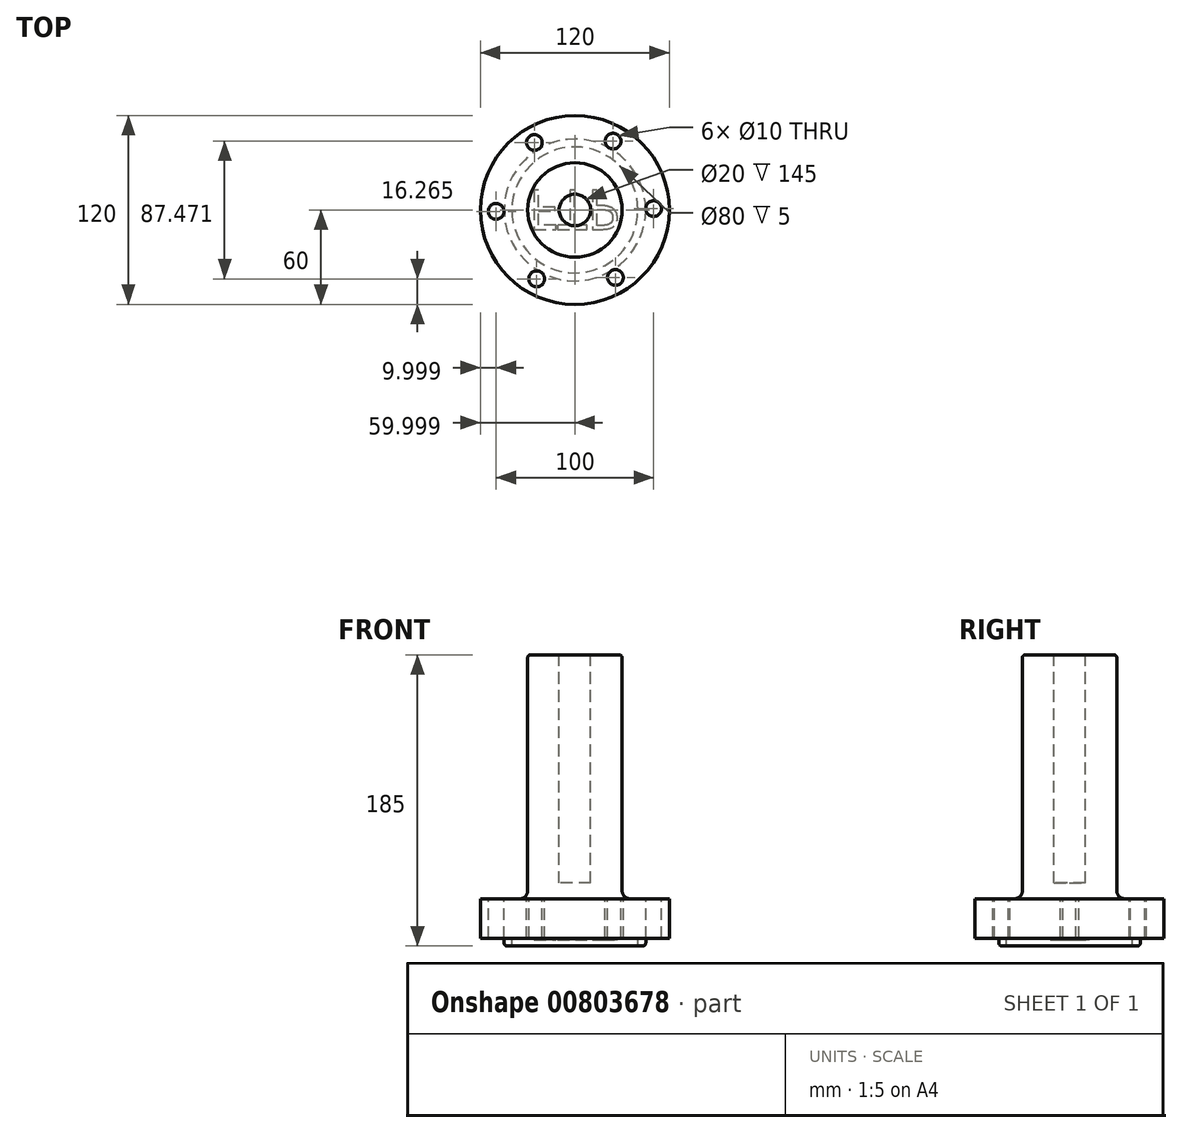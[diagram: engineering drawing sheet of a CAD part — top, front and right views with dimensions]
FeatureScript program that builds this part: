
annotation { "Feature Type Name" : "Feature", "Feature Type Description" : "" }
export const myFeature = defineFeature(function(context is Context, id is Id, definition is map)
    precondition{}
    {
        {
            var Q0;
            Q0=qCreatedBy(makeId("Front.planeOp"),FACE);
            var sketch = newSketch(context, id + "F0", { "sketchPlane" : qUnion([Q0])});
            skLineSegment(sketch, "E0", {"start": v(158.82, 97.64) * mm, "end": v(158.82, -82.36) * mm});
            skLineSegment(sketch, "E1", {"start": v(158.82, -82.36) * mm, "end": v(218.82, -82.36) * mm});
            skLineSegment(sketch, "E2", {"start": v(218.82, -82.36) * mm, "end": v(218.82, -57.36) * mm});
            skLineSegment(sketch, "E3", {"start": v(218.82, -57.36) * mm, "end": v(188.82, -57.36) * mm});
            skLineSegment(sketch, "E4", {"start": v(188.82, -57.36) * mm, "end": v(188.82, 97.64) * mm});
            skLineSegment(sketch, "E5", {"start": v(188.82, 97.64) * mm, "end": v(158.82, 97.64) * mm});
            skSolve(sketch);
        }
        {
            var Q0;
            Q0 = qSketchRegion(id + "F0", true);
            var Q1;
            Q1=sQuery(id+"F0.wireOp",EDGE,"E0");
            revolve(context, id + "F1", {"surfaceOperationType" : NewSurfaceOperationType.NEW, "entities" : qUnion([Q0]), "axis" : qUnion([Q1]), "revolveType" : RevolveType.FULL});
        }
        {
            var Q0;
            Q0=makeQuery(id+"F1.opRevolve","SWEPT_FACE",FACE,{"disambiguationData":[OSD([sQuery(id+"F0.wireOp",EDGE,"E5")])]});
            var sketch = newSketch(context, id + "F2", { "sketchPlane" : qUnion([Q0])});
            skCircle(sketch, "E6", {"center": v(158.82, 0) * mm, "radius": 10 * mm});
            skSolve(sketch);
        }
        {
            var Q0;
            Q0 = qSketchRegion(id + "F2", true);
            extrude(context, id + "F3", {"entities" : qUnion([Q0]), "operationType" : NewBodyOperationType.REMOVE, "oppositeDirection" : true, "depth" : 145 * mm, "offsetDistance" : 25 * mm});
        }
        {
            var Q0;
            Q0=makeQuery(id+"F1.opRevolve","SWEPT_FACE",FACE,{"disambiguationData":[OSD([sQuery(id+"F0.wireOp",EDGE,"E3")])]});
            var sketch = newSketch(context, id + "F4", { "sketchPlane" : qUnion([Q0])});
            skCircle(sketch, "E7", {"center": v(133.07, 42.87) * mm, "radius": 5 * mm});
            skCircle(sketch, "E8.1.0", {"center": v(108.82, -0.87) * mm, "radius": 5 * mm});
            skCircle(sketch, "E8.2.0", {"center": v(134.57, -43.74) * mm, "radius": 5 * mm});
            skCircle(sketch, "E8.3.0", {"center": v(184.57, -42.87) * mm, "radius": 5 * mm});
            skCircle(sketch, "E8.4.0", {"center": v(208.82, 0.87) * mm, "radius": 5 * mm});
            skCircle(sketch, "E8.5.0", {"center": v(183.07, 43.74) * mm, "radius": 5 * mm});
            skPoint(sketch, "E8.center", {"position": v(158.82, 0) * mm});
            skCircle(sketch, "E9", {"center": v(158.82, 0) * mm, "radius": 35 * mm});
            skSolve(sketch);
        }
        {
            var Q0;
            Q0=makeQuery(id+"F4.imprint","IMPRINT",FACE,{"disambiguationData":[TD([[makeQuery(id+"F4.imprint","IMPRINT",EDGE,{"derivedFrom":sQuery(id+"F4.wireOp",EDGE,"E7")}),1.0]])]});
            var Q1;
            Q1=makeQuery(id+"F4.imprint","IMPRINT",FACE,{"disambiguationData":[TD([[makeQuery(id+"F4.imprint","IMPRINT",EDGE,{"derivedFrom":sQuery(id+"F4.wireOp",EDGE,"E8.5.0")}),1.0]])]});
            var Q2;
            Q2=makeQuery(id+"F4.imprint","IMPRINT",FACE,{"disambiguationData":[TD([[makeQuery(id+"F4.imprint","IMPRINT",EDGE,{"derivedFrom":sQuery(id+"F4.wireOp",EDGE,"E8.4.0")}),1.0]])]});
            var Q3;
            Q3=makeQuery(id+"F4.imprint","IMPRINT",FACE,{"disambiguationData":[TD([[makeQuery(id+"F4.imprint","IMPRINT",EDGE,{"derivedFrom":sQuery(id+"F4.wireOp",EDGE,"E8.3.0")}),1.0]])]});
            var Q4;
            Q4=makeQuery(id+"F4.imprint","IMPRINT",FACE,{"disambiguationData":[TD([[makeQuery(id+"F4.imprint","IMPRINT",EDGE,{"derivedFrom":sQuery(id+"F4.wireOp",EDGE,"E8.1.0")}),1.0]])]});
            var Q5;
            Q5=makeQuery(id+"F4.imprint","IMPRINT",FACE,{"disambiguationData":[TD([[makeQuery(id+"F4.imprint","IMPRINT",EDGE,{"derivedFrom":sQuery(id+"F4.wireOp",EDGE,"E8.2.0")}),1.0]])]});
            var Q6;
            Q6=sQuery(id+"F4.wireOp",EDGE,"E7");
            var Q7;
            Q7=sQuery(id+"F4.wireOp",EDGE,"E8.5.0");
            var Q8;
            Q8=sQuery(id+"F4.wireOp",EDGE,"E8.4.0");
            var Q9;
            Q9=sQuery(id+"F4.wireOp",EDGE,"E8.3.0");
            var Q10;
            Q10=sQuery(id+"F4.wireOp",EDGE,"E8.2.0");
            var Q11;
            Q11=sQuery(id+"F4.wireOp",EDGE,"E8.1.0");
            extrude(context, id + "F5", {"entities" : qUnion([Q0, Q1, Q2, Q3, Q4, Q5]), "operationType" : NewBodyOperationType.REMOVE, "surfaceEntities" : qUnion([Q6, Q7, Q8, Q9, Q10, Q11]), "oppositeDirection" : true, "depth" : 25 * mm, "offsetDistance" : 25 * mm});
        }
        {
            var Q0;
            Q0=makeQuery(id+"F1.opRevolve","SWEPT_FACE",FACE,{"disambiguationData":[OSD([sQuery(id+"F0.wireOp",EDGE,"E1")])]});
            var sketch = newSketch(context, id + "F6", { "sketchPlane" : qUnion([Q0])});
            skCircle(sketch, "E10", {"center": v(158.82, 0) * mm, "radius": 45 * mm});
            skCircle(sketch, "E11", {"center": v(158.82, 0) * mm, "radius": 40 * mm});
            skSolve(sketch);
        }
        {
            var Q0;
            Q0=makeQuery(id+"F6.imprint","IMPRINT",FACE,{"disambiguationData":[TD([[makeQuery(id+"F6.imprint","IMPRINT",EDGE,{"derivedFrom":sQuery(id+"F6.wireOp",EDGE,"E10")}),1.0]])]});
            extrude(context, id + "F7", {"entities" : qUnion([Q0]), "operationType" : NewBodyOperationType.ADD, "depth" : 5 * mm, "offsetDistance" : 25 * mm});
        }
        {
            var Q0;
            Q0=makeQuery(id+"F1.opRevolve","SWEPT_EDGE",EDGE,{"disambiguationData":[OSD([sQuery(id+"F0.wireOp",EDGE,"E3"),sQuery(id+"F0.wireOp",EDGE,"E4")])]});
            fillet(context, id + "F8", {"entities" : qUnion([Q0]), "radius" : 5 * mm, "tangentPropagation" : true, "allowEdgeOverflow" : false});
        }
        {
            var Q0;
            Q0=makeQuery(id+"F1.opRevolve","SWEPT_EDGE",EDGE,{"disambiguationData":[OSD([sQuery(id+"F0.wireOp",EDGE,"E4"),sQuery(id+"F0.wireOp",EDGE,"E5")])]});
            fillet(context, id + "F9", {"entities" : qUnion([Q0]), "radius" : 2 * mm, "tangentPropagation" : true, "allowEdgeOverflow" : false});
        }
        {
            var Q0;
            Q0=makeQuery(id+"F7.opExtrude","CAP_EDGE",EDGE,{"disambiguationData":[OSD([sQuery(id+"F6.wireOp",EDGE,"E10")])],"isStart":false});
            fillet(context, id + "F10", {"entities" : qUnion([Q0]), "radius" : 2 * mm, "tangentPropagation" : true, "allowEdgeOverflow" : false});
        }
        {
            var Q0;
            Q0=makeQuery(id+"F7.boolean.opBoolean","SPLIT",FACE,{"disambiguationData":[TD([makeQuery(id+"F7.opExtrude","SWEPT_FACE",FACE,{"disambiguationData":[OSD([sQuery(id+"F6.wireOp",EDGE,"E11")])]})])],"derivedFrom":makeQuery(id+"F1.opRevolve","SWEPT_FACE",FACE,{"disambiguationData":[OSD([sQuery(id+"F0.wireOp",EDGE,"E1")])]})});
            var sketch = newSketch(context, id + "F11", { "sketchPlane" : qUnion([Q0])});
            skSolve(sketch);
        }
        {
            var Q0;
            Q0=makeQuery(id+"F11.imprint","IMPRINT",FACE,{"disambiguationData":[TD([[makeQuery(id+"F11.imprint","IMPRINT",EDGE,{"derivedFrom":makeQuery(id+"F7.opExtrude","CAP_EDGE",EDGE,{"disambiguationData":[OSD([sQuery(id+"F6.wireOp",EDGE,"E11")])],"isStart":true})}),1.0]])]});
            var sketch = newSketch(context, id + "F12", { "sketchPlane" : qUnion([Q0])});
            skText(sketch, "E12", { "text": "FTP", "fontName": "OpenSans-Regular.ttf"});
            skPoint(sketch, "E13", {"position": v(158.82, 0) * mm});
            skPoint(sketch, "E14", {"position": v(129.57, 0) * mm});
            const initialGuessF12  = {"E12": [0.12957, -0.0125, 1, 0, 0.025]};
            skSetInitialGuess(sketch, initialGuessF12);
            skSolve(sketch);
        }
        {
            var Q0;
            Q0 = qSketchRegion(id + "F12", true);
            extrude(context, id + "F13", {"entities" : qUnion([Q0]), "operationType" : NewBodyOperationType.ADD, "depth" : 1 * mm, "offsetDistance" : 25 * mm});
        }
    });
